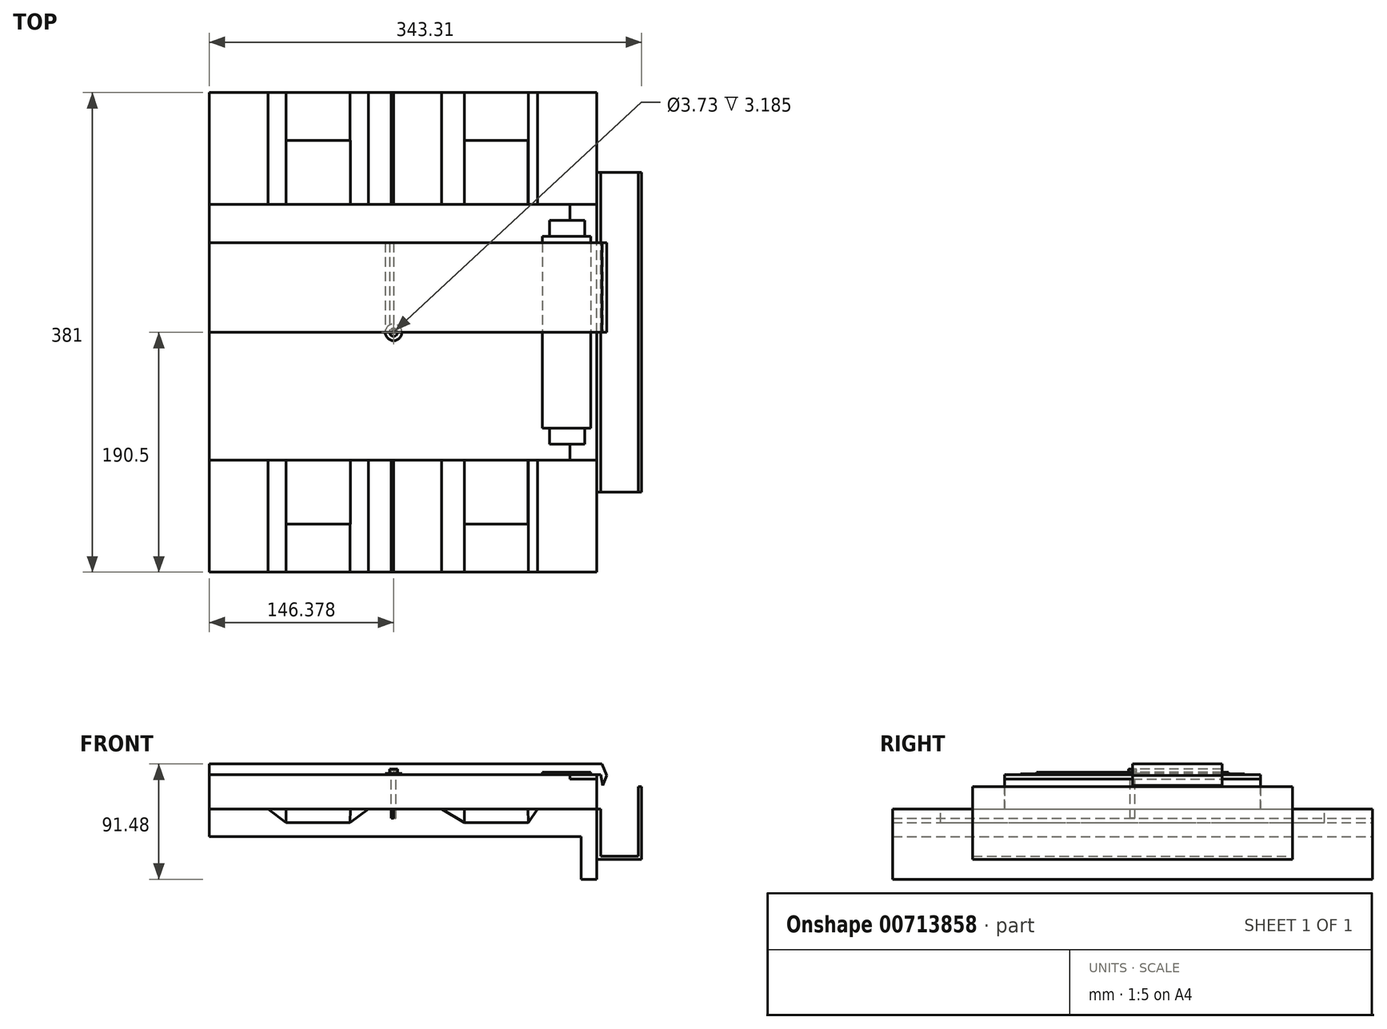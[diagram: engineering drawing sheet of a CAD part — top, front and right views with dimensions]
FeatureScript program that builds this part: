
annotation { "Feature Type Name" : "Feature", "Feature Type Description" : "" }
export const myFeature = defineFeature(function(context is Context, id is Id, definition is map)
    precondition{}
    {
        {
            var Q0;
            Q0=qCreatedBy(makeId("Front.planeOp"),FACE);
            var sketch = newSketch(context, id + "F0", { "sketchPlane" : qUnion([Q0])});
            skLineSegment(sketch, "E0", {"start": v(-173.79, 3.36) * mm, "end": v(-127.13, 3.36) * mm});
            skLineSegment(sketch, "E1", {"start": v(-127.13, 3.36) * mm, "end": v(-112.75, -7.5) * mm});
            skLineSegment(sketch, "E2", {"start": v(-112.75, -7.5) * mm, "end": v(-61.95, -7.5) * mm});
            skLineSegment(sketch, "E3", {"start": v(-61.95, -7.5) * mm, "end": v(-47.65, 3.36) * mm});
            skLineSegment(sketch, "E4", {"start": v(-47.65, 3.36) * mm, "end": v(10.67, 3.36) * mm});
            skLineSegment(sketch, "E5", {"start": v(10.67, 3.36) * mm, "end": v(28.58, -7.5) * mm});
            skLineSegment(sketch, "E6", {"start": v(28.58, -7.5) * mm, "end": v(79.38, -7.5) * mm});
            skLineSegment(sketch, "E7", {"start": v(79.38, -7.5) * mm, "end": v(86.9, 3.36) * mm});
            skLineSegment(sketch, "E8", {"start": v(86.9, 3.36) * mm, "end": v(133.83, 3.36) * mm});
            skLineSegment(sketch, "E9", {"start": v(133.83, 3.36) * mm, "end": v(133.83, -52.52) * mm});
            skLineSegment(sketch, "E10", {"start": v(133.83, 3.36) * mm, "end": v(136.82, 3.36) * mm});
            skLineSegment(sketch, "E11", {"start": v(136.82, 3.36) * mm, "end": v(136.82, -34.1) * mm});
            skLineSegment(sketch, "E12", {"start": v(136.82, -34.1) * mm, "end": v(166.79, -34.1) * mm});
            skLineSegment(sketch, "E13", {"start": v(166.79, -34.1) * mm, "end": v(166.79, 21.11) * mm});
            skLineSegment(sketch, "E14", {"start": v(166.79, 21.11) * mm, "end": v(169.42, 21.11) * mm});
            skLineSegment(sketch, "E15", {"start": v(169.42, 21.11) * mm, "end": v(169.42, -36.72) * mm});
            skLineSegment(sketch, "E16", {"start": v(169.42, -36.72) * mm, "end": v(133.83, -36.72) * mm});
            skLineSegment(sketch, "E17", {"start": v(-112.75, -7.5) * mm, "end": v(-112.75, 3.36) * mm});
            skLineSegment(sketch, "E18", {"start": v(-112.75, 3.36) * mm, "end": v(-61.92, 3.36) * mm});
            skLineSegment(sketch, "E19", {"start": v(-61.92, 3.36) * mm, "end": v(-61.95, -7.5) * mm});
            skLineSegment(sketch, "E20", {"start": v(28.58, -7.5) * mm, "end": v(28.58, 3.36) * mm});
            skLineSegment(sketch, "E21", {"start": v(28.58, 3.36) * mm, "end": v(79.25, 3.36) * mm});
            skLineSegment(sketch, "E22", {"start": v(79.25, 3.36) * mm, "end": v(79.38, -7.5) * mm});
            skLineSegment(sketch, "E23", {"start": v(-173.79, 3.36) * mm, "end": v(-173.79, 30.58) * mm});
            skLineSegment(sketch, "E24", {"start": v(-173.79, 30.58) * mm, "end": v(133.83, 30.58) * mm});
            skLineSegment(sketch, "E25", {"start": v(133.83, 30.58) * mm, "end": v(133.83, 3.36) * mm});
            skLineSegment(sketch, "E26", {"start": v(-127.13, 3.36) * mm, "end": v(-112.75, 3.36) * mm});
            skLineSegment(sketch, "E27", {"start": v(-61.92, 3.36) * mm, "end": v(-47.65, 3.36) * mm});
            skLineSegment(sketch, "E28", {"start": v(10.67, 3.36) * mm, "end": v(28.58, 3.36) * mm});
            skLineSegment(sketch, "E29", {"start": v(79.25, 3.36) * mm, "end": v(86.9, 3.36) * mm});
            skLineSegment(sketch, "E30", {"start": v(112.64, 30.58) * mm, "end": v(112.64, 27.16) * mm});
            skLineSegment(sketch, "E31", {"start": v(112.64, 27.16) * mm, "end": v(133.83, 27.16) * mm});
            skLineSegment(sketch, "E32", {"start": v(133.83, 27.16) * mm, "end": v(133.83, 30.58) * mm});
            skLineSegment(sketch, "E33", {"start": v(133.83, 30.58) * mm, "end": v(136.82, 30.58) * mm});
            skLineSegment(sketch, "E34", {"start": v(136.82, 30.58) * mm, "end": v(142.34, 3.36) * mm});
            skLineSegment(sketch, "E35", {"start": v(142.34, 3.36) * mm, "end": v(139.71, 3.36) * mm});
            skLineSegment(sketch, "E36", {"start": v(139.71, 3.36) * mm, "end": v(133.83, 27.16) * mm});
            skLineSegment(sketch, "E37", {"start": v(96.34, 30.58) * mm, "end": v(96.34, 31.29) * mm});
            skLineSegment(sketch, "E38", {"start": v(96.34, 31.29) * mm, "end": v(124.28, 31.29) * mm});
            skLineSegment(sketch, "E39", {"start": v(124.28, 31.29) * mm, "end": v(124.28, 30.58) * mm});
            skLineSegment(sketch, "E40", {"start": v(90.49, 30.58) * mm, "end": v(90.49, 32.3) * mm});
            skLineSegment(sketch, "E41", {"start": v(90.49, 32.3) * mm, "end": v(129.1, 32.3) * mm});
            skLineSegment(sketch, "E42", {"start": v(129.1, 32.3) * mm, "end": v(129.1, 30.58) * mm});
            skLineSegment(sketch, "E43", {"start": v(-29.38, 33.76) * mm, "end": v(-29.38, -4.05) * mm});
            skLineSegment(sketch, "E44", {"start": v(-34.14, 30.58) * mm, "end": v(-34.14, 31.6) * mm});
            skLineSegment(sketch, "E45", {"start": v(-34.14, 31.6) * mm, "end": v(-30.64, 31.6) * mm});
            skLineSegment(sketch, "E46", {"start": v(-30.64, 31.6) * mm, "end": v(-30.64, 34.96) * mm});
            skLineSegment(sketch, "E47", {"start": v(-173.79, 30.58) * mm, "end": v(-173.79, 38.96) * mm});
            skLineSegment(sketch, "E48", {"start": v(-173.79, 38.96) * mm, "end": v(137.87, 38.96) * mm});
            skLineSegment(sketch, "E49", {"start": v(137.87, 38.96) * mm, "end": v(141.83, 29.8) * mm});
            skLineSegment(sketch, "E50", {"start": v(141.83, 29.8) * mm, "end": v(138.55, 22.03) * mm});
            skLineSegment(sketch, "E51", {"start": v(133.83, -52.52) * mm, "end": v(121.46, -52.52) * mm});
            skLineSegment(sketch, "E52", {"start": v(121.46, -52.52) * mm, "end": v(121.46, -18.76) * mm});
            skLineSegment(sketch, "E53", {"start": v(121.46, -18.76) * mm, "end": v(-173.9, -18.76) * mm});
            skLineSegment(sketch, "E54", {"start": v(-173.9, -18.76) * mm, "end": v(-173.79, 3.36) * mm});
            skLineSegment(sketch, "E55", {"start": v(-27.51, 38.96) * mm, "end": v(-27.51, -9.38) * mm, "construction": true});
            skPoint(sketch, "E55.startSnap0", {"position": v(-27.51, 33.76) * mm});
            skLineSegment(sketch, "E56", {"start": v(-30.64, 34.96) * mm, "end": v(-27.51, 34.96) * mm});
            skLineSegment(sketch, "E57", {"start": v(-29.38, 33.76) * mm, "end": v(-27.51, 33.76) * mm});
            skLineSegment(sketch, "E58", {"start": v(-29.38, -4.05) * mm, "end": v(-27.51, -4.05) * mm});
            skLineSegment(sketch, "E59", {"start": v(-27.51, 33.76) * mm, "end": v(-27.51, -4.05) * mm});
            skLineSegment(sketch, "E60", {"start": v(-27.51, 34.96) * mm, "end": v(-27.51, 33.76) * mm});
            skSolve(sketch);
        }
        {
            var Q0;
            Q0=makeQuery(id+"F0.imprint","IMPRINT",FACE,{"disambiguationData":[TD([[makeQuery(id+"F0.imprint","IMPRINT",EDGE,{"derivedFrom":sQuery(id+"F0.wireOp",EDGE,"E0")}),-1.0]])]});
            extrude(context, id + "F1", {"entities" : qUnion([Q0]), "endBound" : BoundingType.SYMMETRIC, "depth" : 381 * mm});
        }
        {
            var Q0;
            Q0=makeQuery(id+"F0.imprint","IMPRINT",FACE,{"disambiguationData":[TD([[makeQuery(id+"F0.imprint","IMPRINT",EDGE,{"derivedFrom":sQuery(id+"F0.wireOp",EDGE,"E2")}),1.0]])]});
            var Q1;
            Q1=makeQuery(id+"F0.imprint","IMPRINT",FACE,{"disambiguationData":[TD([[makeQuery(id+"F0.imprint","IMPRINT",EDGE,{"derivedFrom":sQuery(id+"F0.wireOp",EDGE,"E6")}),1.0]])]});
            extrude(context, id + "F2", {"entities" : qUnion([Q0, Q1]), "endBound" : BoundingType.SYMMETRIC, "depth" : 304.8 * mm});
        }
        {
            var Q0;
            Q0=makeQuery(id+"F0.imprint","IMPRINT",FACE,{"disambiguationData":[TD([[makeQuery(id+"F0.imprint","IMPRINT",EDGE,{"derivedFrom":sQuery(id+"F0.wireOp",EDGE,"E8")}),1.0]])]});
            var Q1;
            Q1=makeQuery(id+"F0.imprint","IMPRINT",FACE,{"disambiguationData":[TD([[makeQuery(id+"F0.imprint","IMPRINT",EDGE,{"derivedFrom":sQuery(id+"F0.wireOp",EDGE,"E0")}),1.0]])]});
            var Q2;
            {var subQ0=sQuery(id+"F0.wireOp",EDGE,"E43");var subQ1=sQuery(id+"F0.wireOp",EDGE,"E4");var subQ2=makeQuery(id+"F0.imprint","INTERSECT",VERTEX,{"derivedFrom":[subQ1,subQ0]});Q2=makeQuery(id+"F0.imprint","IMPRINT",FACE,{"disambiguationData":[TD([[makeQuery(id+"F0.imprint","IMPRINT",EDGE,{"disambiguationData":[TD([[subQ2,-1.0]])],"derivedFrom":subQ1}),1.0]])]});}
            extrude(context, id + "F3", {"entities" : qUnion([Q0, Q1, Q2]), "endBound" : BoundingType.SYMMETRIC, "depth" : 203.2 * mm});
        }
        {
            var Q0;
            {var subQ5=sQuery(id+"F0.wireOp",EDGE,"E57");Q0=makeQuery(id+"F0.imprint","IMPRINT",FACE,{"disambiguationData":[TD([[makeQuery(id+"F0.imprint","IMPRINT",EDGE,{"derivedFrom":subQ5}),-1.0]])]});}
            var Q1;
            {var subQ0=sQuery(id+"F0.wireOp",EDGE,"E43");var subQ1=sQuery(id+"F0.wireOp",EDGE,"E4");var subQ2=makeQuery(id+"F0.imprint","INTERSECT",VERTEX,{"derivedFrom":[subQ1,subQ0]});Q1=makeQuery(id+"F0.imprint","IMPRINT",FACE,{"disambiguationData":[TD([[makeQuery(id+"F0.imprint","IMPRINT",EDGE,{"disambiguationData":[TD([[subQ2,-1.0]])],"derivedFrom":subQ1}),1.0]])]});}
            var Q2;
            {var subQ5=sQuery(id+"F0.wireOp",EDGE,"E58");Q2=makeQuery(id+"F0.imprint","IMPRINT",FACE,{"disambiguationData":[TD([[makeQuery(id+"F0.imprint","IMPRINT",EDGE,{"derivedFrom":subQ5}),1.0]])]});}
            var Q3;
            Q3=sQuery(id+"F0.wireOp",EDGE,"E55");
            revolve(context, id + "F4", {"entities" : qUnion([Q0, Q1, Q2]), "axis" : qUnion([Q3]), "revolveType" : RevolveType.FULL});
        }
        {
            var Q0;
            {var subQ4=sQuery(id+"F0.wireOp",EDGE,"E44");Q0=makeQuery(id+"F0.imprint","IMPRINT",FACE,{"disambiguationData":[TD([[makeQuery(id+"F0.imprint","IMPRINT",EDGE,{"derivedFrom":subQ4}),-1.0]])]});}
            var Q1;
            Q1=sQuery(id+"F0.wireOp",EDGE,"E55");
            revolve(context, id + "F5", {"entities" : qUnion([Q0]), "axis" : qUnion([Q1]), "revolveType" : RevolveType.FULL});
        }
        {
            var Q0;
            {var subQ0=sQuery(id+"F0.wireOp",EDGE,"E10");Q0=makeQuery(id+"F0.imprint","IMPRINT",FACE,{"disambiguationData":[TD([[makeQuery(id+"F0.imprint","IMPRINT",EDGE,{"derivedFrom":subQ0}),-1.0]])]});}
            extrude(context, id + "F6", {"entities" : qUnion([Q0]), "endBound" : BoundingType.SYMMETRIC, "depth" : 254 * mm});
        }
        {
            var Q0;
            {var subQ0=sQuery(id+"F0.wireOp",EDGE,"E30");Q0=makeQuery(id+"F0.imprint","IMPRINT",FACE,{"disambiguationData":[TD([[makeQuery(id+"F0.imprint","IMPRINT",EDGE,{"derivedFrom":subQ0}),1.0]])]});}
            var Q1;
            Q1=makeQuery(id+"F0.imprint","IMPRINT",FACE,{"disambiguationData":[TD([[makeQuery(id+"F0.imprint","IMPRINT",EDGE,{"derivedFrom":sQuery(id+"F0.wireOp",EDGE,"E32")}),-1.0]])]});
            extrude(context, id + "F7", {"entities" : qUnion([Q0, Q1]), "endBound" : BoundingType.SYMMETRIC, "depth" : 203.2 * mm});
        }
        {
            var Q0;
            {var subQ0=sQuery(id+"F0.wireOp",EDGE,"E37");Q0=makeQuery(id+"F0.imprint","IMPRINT",FACE,{"disambiguationData":[TD([[makeQuery(id+"F0.imprint","IMPRINT",EDGE,{"derivedFrom":subQ0}),-1.0]])]});}
            extrude(context, id + "F8", {"entities" : qUnion([Q0]), "endBound" : BoundingType.SYMMETRIC, "depth" : 177.8 * mm});
        }
        {
            var Q0;
            {var subQ0=sQuery(id+"F0.wireOp",EDGE,"E37");Q0=makeQuery(id+"F0.imprint","IMPRINT",FACE,{"disambiguationData":[TD([[makeQuery(id+"F0.imprint","IMPRINT",EDGE,{"derivedFrom":subQ0}),1.0]])]});}
            extrude(context, id + "F9", {"entities" : qUnion([Q0]), "endBound" : BoundingType.SYMMETRIC, "depth" : 152.4 * mm});
        }
        {
            var Q0;
            {var subQ1=sQuery(id+"F0.wireOp",EDGE,"E33");Q0=makeQuery(id+"F0.imprint","IMPRINT",FACE,{"disambiguationData":[TD([[makeQuery(id+"F0.imprint","IMPRINT",EDGE,{"derivedFrom":subQ1}),1.0]])]});}
            extrude(context, id + "F10", {"entities" : qUnion([Q0]), "oppositeDirection" : true, "depth" : 71.12 * mm});
        }
    });
